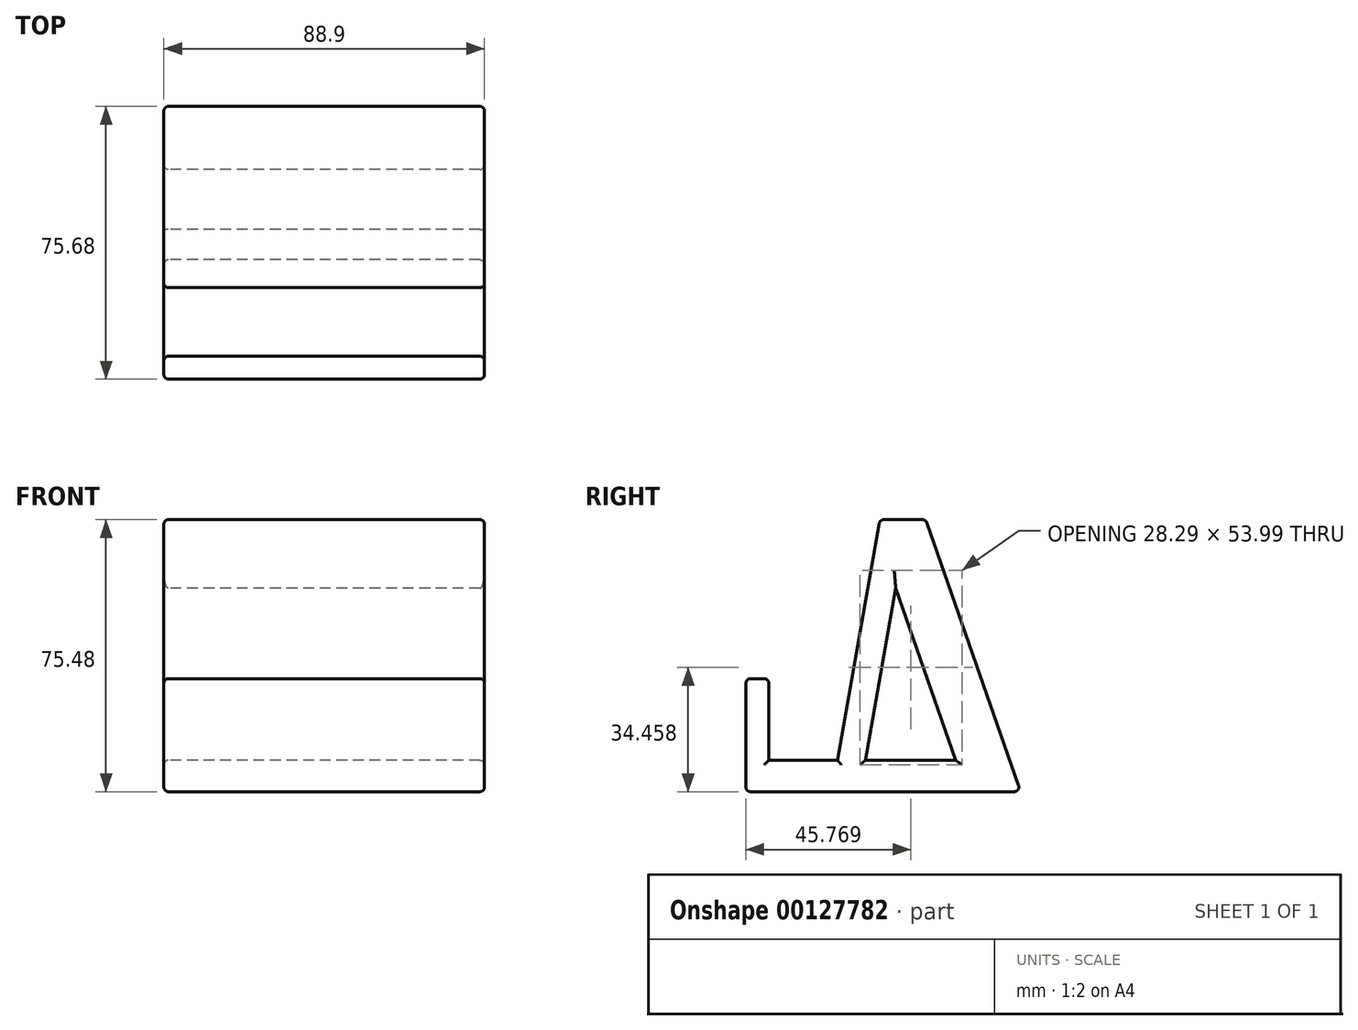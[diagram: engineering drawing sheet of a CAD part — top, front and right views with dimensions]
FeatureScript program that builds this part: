
annotation { "Feature Type Name" : "Feature", "Feature Type Description" : "" }
export const myFeature = defineFeature(function(context is Context, id is Id, definition is map)
    precondition{}
    {
        {
            var Q0;
            Q0=qCreatedBy(makeId("Right.planeOp"),FACE);
            var sketch = newSketch(context, id + "F0", { "sketchPlane" : qUnion([Q0])});
            skLineSegment(sketch, "E0", {"start": v(0, 0) * mm, "end": v(76.2, 0) * mm});
            skLineSegment(sketch, "E1", {"start": v(76.2, 0) * mm, "end": v(49.87, 75.48) * mm});
            skLineSegment(sketch, "E2", {"start": v(49.87, 75.48) * mm, "end": v(37.17, 75.48) * mm});
            skLineSegment(sketch, "E3", {"start": v(37.17, 75.48) * mm, "end": v(25.4, 8.73) * mm});
            skLineSegment(sketch, "E4", {"start": v(25.4, 8.73) * mm, "end": v(6.35, 8.73) * mm});
            skLineSegment(sketch, "E5", {"start": v(6.35, 8.73) * mm, "end": v(6.35, 31.36) * mm});
            skLineSegment(sketch, "E6", {"start": v(6.35, 31.36) * mm, "end": v(0, 31.36) * mm});
            skLineSegment(sketch, "E7", {"start": v(0, 31.36) * mm, "end": v(0, 0) * mm});
            skLineSegment(sketch, "E8", {"start": v(41.55, 56.43) * mm, "end": v(33.14, 8.73) * mm});
            skLineSegment(sketch, "E9", {"start": v(33.14, 8.73) * mm, "end": v(58.13, 8.73) * mm});
            skLineSegment(sketch, "E10", {"start": v(58.13, 8.73) * mm, "end": v(41.55, 56.43) * mm});
            skSolve(sketch);
        }
        {
            var Q0;
            Q0 = qSketchRegion(id + "F0", true);
            extrude(context, id + "F1", {"entities" : qUnion([Q0]), "depth" : 88.9 * mm});
        }
        {
            var Q0;
            Q0=makeQuery(id+"F1.opExtrude","CAP_EDGE",EDGE,{"disambiguationData":[OSD([sQuery(id+"F0.wireOp",EDGE,"E3")])],"isStart":false});
            var Q1;
            Q1=makeQuery(id+"F1.opExtrude","CAP_EDGE",EDGE,{"disambiguationData":[OSD([sQuery(id+"F0.wireOp",EDGE,"E1")])],"isStart":false});
            var Q2;
            Q2=makeQuery(id+"F1.opExtrude","CAP_EDGE",EDGE,{"disambiguationData":[OSD([sQuery(id+"F0.wireOp",EDGE,"E10")])],"isStart":false});
            var Q3;
            Q3=makeQuery(id+"F1.opExtrude","CAP_EDGE",EDGE,{"disambiguationData":[OSD([sQuery(id+"F0.wireOp",EDGE,"E8")])],"isStart":false});
            var Q4;
            Q4=makeQuery(id+"F1.opExtrude","SWEPT_EDGE",EDGE,{"disambiguationData":[OSD([sQuery(id+"F0.wireOp",EDGE,"E1"),sQuery(id+"F0.wireOp",EDGE,"E2")])]});
            var Q5;
            Q5=makeQuery(id+"F1.opExtrude","CAP_EDGE",EDGE,{"disambiguationData":[OSD([sQuery(id+"F0.wireOp",EDGE,"E1")])],"isStart":true});
            var Q6;
            Q6=makeQuery(id+"F1.opExtrude","CAP_FACE",FACE,{"disambiguationData":[OSD([sQuery(id+"F0.wireOp",EDGE,"E0"),sQuery(id+"F0.wireOp",EDGE,"E1"),sQuery(id+"F0.wireOp",EDGE,"E2"),sQuery(id+"F0.wireOp",EDGE,"E3"),sQuery(id+"F0.wireOp",EDGE,"E4"),sQuery(id+"F0.wireOp",EDGE,"E5"),sQuery(id+"F0.wireOp",EDGE,"E6"),sQuery(id+"F0.wireOp",EDGE,"E7"),sQuery(id+"F0.wireOp",EDGE,"E8"),sQuery(id+"F0.wireOp",EDGE,"E9"),sQuery(id+"F0.wireOp",EDGE,"E10")])],"isStart":true});
            var Q7;
            Q7=makeQuery(id+"F1.opExtrude","SWEPT_EDGE",EDGE,{"disambiguationData":[OSD([sQuery(id+"F0.wireOp",EDGE,"E0"),sQuery(id+"F0.wireOp",EDGE,"E7")])]});
            var Q8;
            Q8=makeQuery(id+"F1.opExtrude","SWEPT_EDGE",EDGE,{"disambiguationData":[OSD([sQuery(id+"F0.wireOp",EDGE,"E6"),sQuery(id+"F0.wireOp",EDGE,"E7")])]});
            var Q9;
            Q9=makeQuery(id+"F1.opExtrude","CAP_FACE",FACE,{"disambiguationData":[OSD([sQuery(id+"F0.wireOp",EDGE,"E0"),sQuery(id+"F0.wireOp",EDGE,"E1"),sQuery(id+"F0.wireOp",EDGE,"E2"),sQuery(id+"F0.wireOp",EDGE,"E3"),sQuery(id+"F0.wireOp",EDGE,"E4"),sQuery(id+"F0.wireOp",EDGE,"E5"),sQuery(id+"F0.wireOp",EDGE,"E6"),sQuery(id+"F0.wireOp",EDGE,"E7"),sQuery(id+"F0.wireOp",EDGE,"E8"),sQuery(id+"F0.wireOp",EDGE,"E9"),sQuery(id+"F0.wireOp",EDGE,"E10")])],"isStart":false});
            var Q10;
            Q10=makeQuery(id+"F1.opExtrude","SWEPT_EDGE",EDGE,{"disambiguationData":[OSD([sQuery(id+"F0.wireOp",EDGE,"E5"),sQuery(id+"F0.wireOp",EDGE,"E6")])]});
            var Q11;
            Q11=makeQuery(id+"F1.opExtrude","SWEPT_EDGE",EDGE,{"disambiguationData":[OSD([sQuery(id+"F0.wireOp",EDGE,"E2"),sQuery(id+"F0.wireOp",EDGE,"E3")])]});
            var Q12;
            Q12=makeQuery(id+"F1.opExtrude","SWEPT_FACE",FACE,{"disambiguationData":[OSD([sQuery(id+"F0.wireOp",EDGE,"E1")])]});
            fillet(context, id + "F2", {"entities" : qUnion([Q0, Q1, Q2, Q3, Q4, Q5, Q6, Q7, Q8, Q9, Q10, Q11, Q12]), "radius" : 1.27 * mm, "tangentPropagation" : true, "allowEdgeOverflow" : false});
        }
    });
